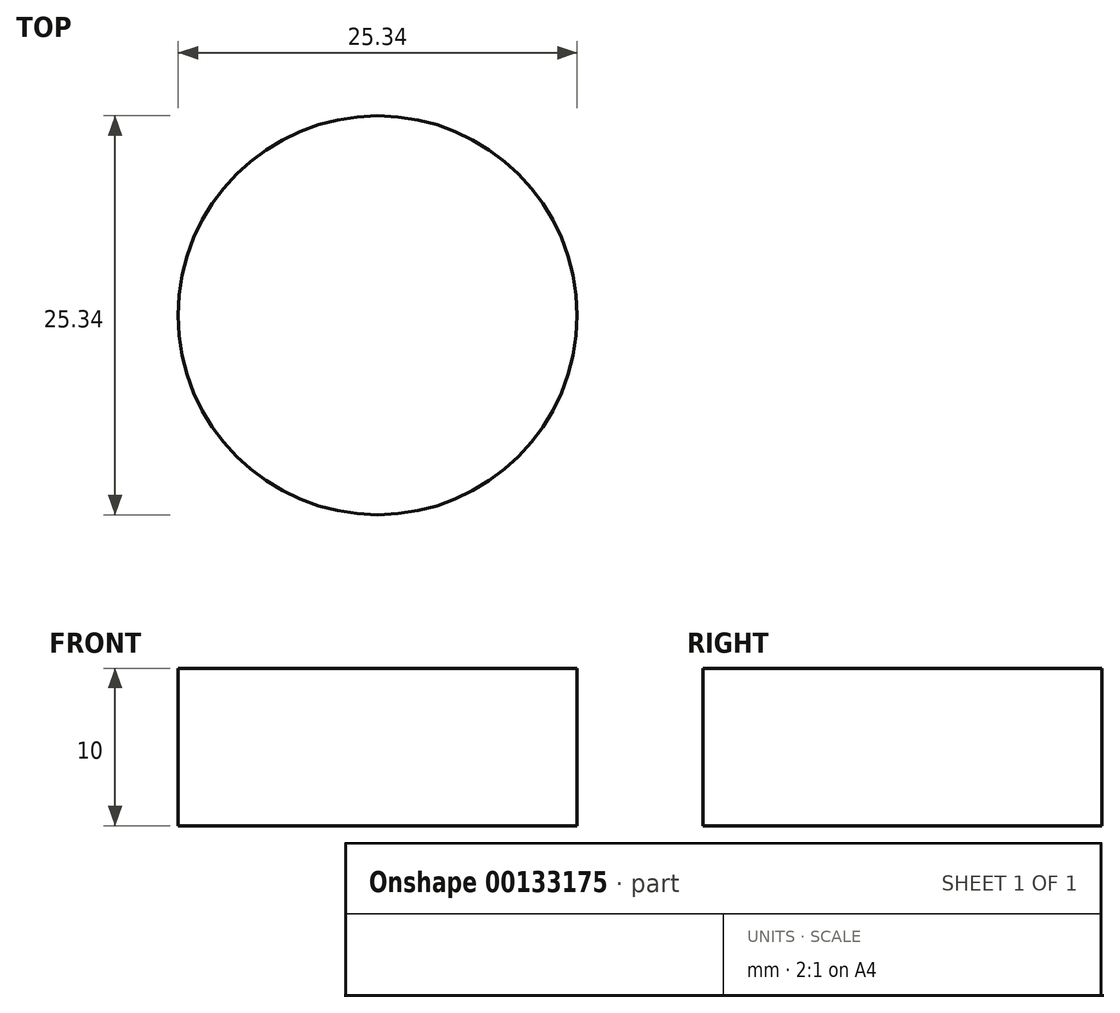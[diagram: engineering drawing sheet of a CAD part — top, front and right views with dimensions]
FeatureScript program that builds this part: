
annotation { "Feature Type Name" : "Feature", "Feature Type Description" : "" }
export const myFeature = defineFeature(function(context is Context, id is Id, definition is map)
    precondition{}
    {
        {
            var Q0;
            Q0=qCreatedBy(makeId("Top.planeOp"),FACE);
            var sketch = newSketch(context, id + "F0", { "sketchPlane" : qUnion([Q0])});
            skCircle(sketch, "E0", {"center": v(0, 0) * mm, "radius": 12.67 * mm});
            skSolve(sketch);
        }
        {
            var Q0;
            Q0=makeQuery(id+"F0.imprint","IMPRINT",FACE,{"disambiguationData":[TD([[makeQuery(id+"F0.imprint","IMPRINT",EDGE,{"derivedFrom":sQuery(id+"F0.wireOp",EDGE,"E0")}),1.0]])]});
            extrude(context, id + "F1", {"entities" : qUnion([Q0]), "depth" : 10 * mm});
        }
    });
